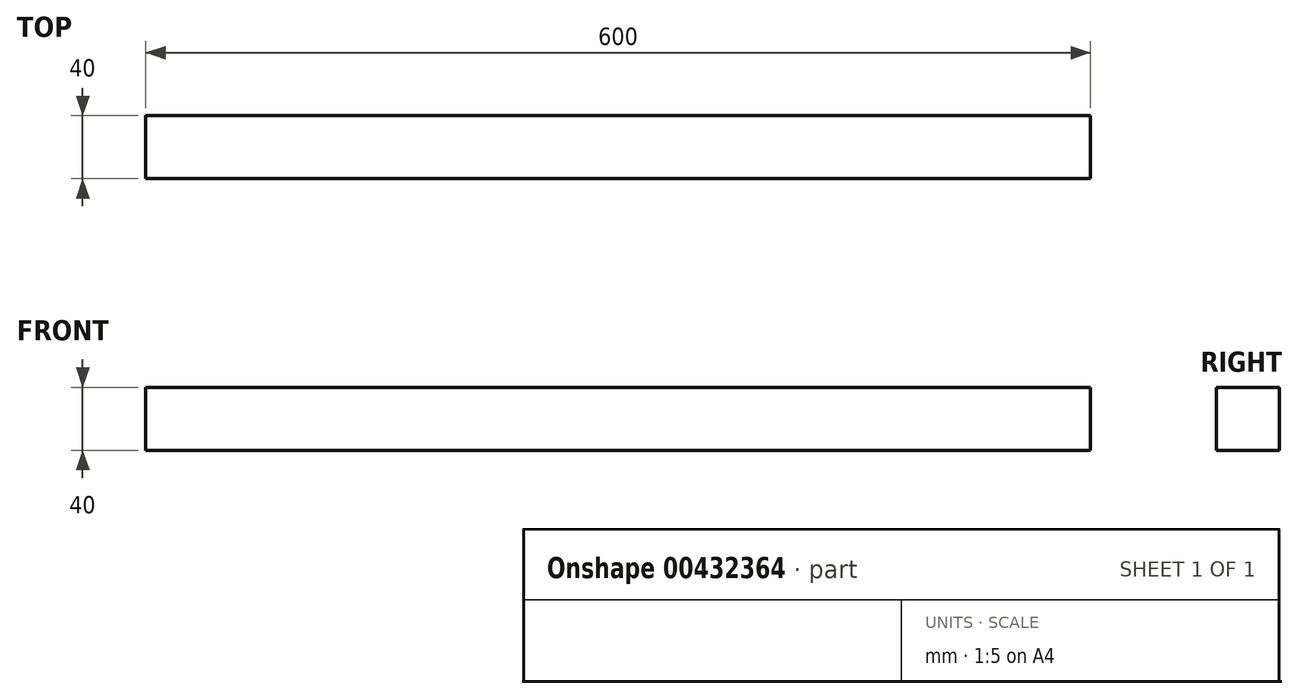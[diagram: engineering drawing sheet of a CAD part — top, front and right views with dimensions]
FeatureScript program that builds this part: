
annotation { "Feature Type Name" : "Feature", "Feature Type Description" : "" }
export const myFeature = defineFeature(function(context is Context, id is Id, definition is map)
    precondition{}
    {
        {
            var Q0;
            Q0=qCreatedBy(makeId("Front.planeOp"),FACE);
            var sketch = newSketch(context, id + "F0", { "sketchPlane" : qUnion([Q0])});
            skLineSegment(sketch, "E0.bottom", {"start": v(-300, 20) * mm, "end": v(300, 20) * mm});
            skLineSegment(sketch, "E0.top", {"start": v(-300, -20) * mm, "end": v(300, -20) * mm});
            skLineSegment(sketch, "E0.left", {"start": v(-300, 20) * mm, "end": v(-300, -20) * mm});
            skLineSegment(sketch, "E0.right", {"start": v(300, 20) * mm, "end": v(300, -20) * mm});
            skPoint(sketch, "E0.middle", {"position": v(0, 0) * mm});
            skSolve(sketch);
        }
        {
            var Q0;
            Q0 = qSketchRegion(id + "F0", true);
            extrude(context, id + "F1", {"entities" : qUnion([Q0]), "endBound" : BoundingType.SYMMETRIC, "depth" : 40 * mm});
        }
    });
